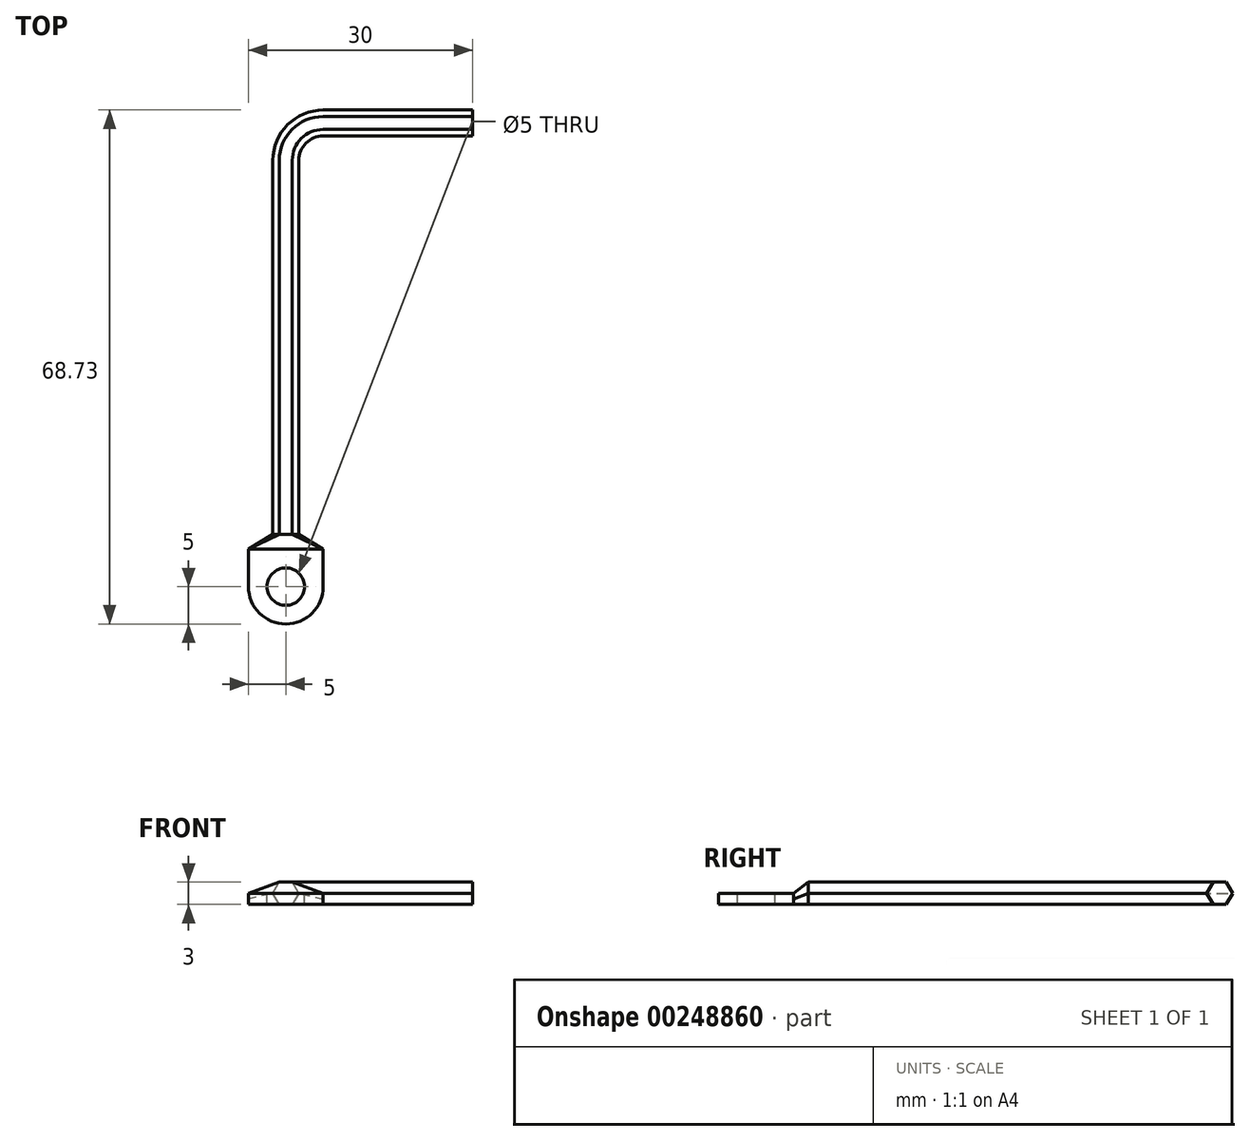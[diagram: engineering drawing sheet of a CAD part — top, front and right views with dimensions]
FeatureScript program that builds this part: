
annotation { "Feature Type Name" : "Feature", "Feature Type Description" : "" }
export const myFeature = defineFeature(function(context is Context, id is Id, definition is map)
    precondition{}
    {
        {
            var Q0;
            Q0=qCreatedBy(makeId("Front.planeOp"),FACE);
            var sketch = newSketch(context, id + "F0", { "sketchPlane" : qUnion([Q0])});
            skCircle(sketch, "E0.cCircle", {"center": v(0, 0) * mm, "radius": 1.5 * mm, "construction": true});
            skLineSegment(sketch, "E0.0", {"start": v(0.87, -1.5) * mm, "end": v(-0.87, -1.5) * mm});
            skLineSegment(sketch, "E0.1", {"start": v(-0.87, -1.5) * mm, "end": v(-1.73, 0) * mm});
            skLineSegment(sketch, "E0.2", {"start": v(-1.73, 0) * mm, "end": v(-0.87, 1.5) * mm});
            skLineSegment(sketch, "E0.3", {"start": v(-0.87, 1.5) * mm, "end": v(0.87, 1.5) * mm});
            skLineSegment(sketch, "E0.4", {"start": v(0.87, 1.5) * mm, "end": v(1.73, 0) * mm});
            skLineSegment(sketch, "E0.5", {"start": v(1.73, 0) * mm, "end": v(0.87, -1.5) * mm});
            skPoint(sketch, "E0.0.midPoint", {"position": v(0, -1.5) * mm});
            skSolve(sketch);
        }
        {
            var Q0;
            Q0=qCreatedBy(makeId("Top.planeOp"),FACE);
            var sketch = newSketch(context, id + "F1", { "sketchPlane" : qUnion([Q0])});
            skLineSegment(sketch, "E1", {"start": v(0, 0) * mm, "end": v(0, 50) * mm});
            skLineSegment(sketch, "E2", {"start": v(5, 55) * mm, "end": v(25, 55) * mm});
            skPoint(sketch, "E3.visualSharp", {"position": v(0, 55) * mm});
            skArc(sketch, "E3.filletArc", {"start": v(5, 55) * mm, "mid": v(1.46, 53.54) * mm, "end": v(0, 50) * mm});
            skSolve(sketch);
        }
        {
            var Q0;
            Q0 = qSketchRegion(id + "F0", true);
            var Q1;
            Q1 = qConstructionFilter(qBodyType(qCreatedBy(id + "F1" ,EDGE), BodyType.WIRE), ConstructionObject.NO);
            sweep(context, id + "F2", {"profiles" : qUnion([Q0]), "path" : qUnion([Q1])});
        }
        {
            var Q0;
            Q0=makeQuery(id+"F2.opSweep","CAP_FACE",FACE,{"disambiguationData":[OSD([sQuery(id+"F0.wireOp",EDGE,"E0.0"),sQuery(id+"F0.wireOp",EDGE,"E0.1"),sQuery(id+"F0.wireOp",EDGE,"E0.2"),sQuery(id+"F0.wireOp",EDGE,"E0.3"),sQuery(id+"F0.wireOp",EDGE,"E0.4"),sQuery(id+"F0.wireOp",EDGE,"E0.5"),sQuery(id+"F1.wireOp",VERTEX,"E1.start")])],"isStart":true});
            cPlane(context, id + "F3", {"entities" : qUnion([Q0]), "cplaneType" : CPlaneType.OFFSET, "offset" : 2 * mm, "width" : 150 * mm, "height" : 150 * mm});
        }
        {
            var Q0;
            Q0=qCreatedBy(id+"F3.planeOp",FACE);
            var sketch = newSketch(context, id + "F4", { "sketchPlane" : qUnion([Q0])});
            skLineSegment(sketch, "E4.bottom", {"start": v(-5, 0) * mm, "end": v(5, 0) * mm});
            skLineSegment(sketch, "E4.top", {"start": v(-5, -1.5) * mm, "end": v(5, -1.5) * mm});
            skLineSegment(sketch, "E4.left", {"start": v(-5, 0) * mm, "end": v(-5, -1.5) * mm});
            skLineSegment(sketch, "E4.right", {"start": v(5, 0) * mm, "end": v(5, -1.5) * mm});
            skSolve(sketch);
        }
        {
            var Q0;
            Q0 = qSketchRegion(id + "F4", true);
            extrude(context, id + "F5", {"entities" : qUnion([Q0]), "depth" : 10 * mm});
        }
        {
            var Q0;
            Q0=makeQuery(id+"F5.opExtrude","SWEPT_FACE",FACE,{"disambiguationData":[OSD([sQuery(id+"F4.wireOp",EDGE,"E4.bottom")])]});
            var sketch = newSketch(context, id + "F6", { "sketchPlane" : qUnion([Q0])});
            skCircle(sketch, "E5", {"center": v(0, -7) * mm, "radius": 2.5 * mm});
            skPoint(sketch, "E5.centerSnap0", {"position": v(-5, -7) * mm});
            skPoint(sketch, "E5.centerSnap1", {"position": v(0, -12) * mm});
            skSolve(sketch);
        }
        {
            var Q0;
            Q0 = qSketchRegion(id + "F6", true);
            extrude(context, id + "F7", {"entities" : qUnion([Q0]), "operationType" : NewBodyOperationType.REMOVE, "oppositeDirection" : true, "depth" : 25 * mm});
        }
        {
            var Q0;
            Q0=makeQuery(id+"F5.opExtrude","CAP_FACE",FACE,{"disambiguationData":[OSD([sQuery(id+"F4.wireOp",EDGE,"E4.bottom"),sQuery(id+"F4.wireOp",EDGE,"E4.top"),sQuery(id+"F4.wireOp",EDGE,"E4.left"),sQuery(id+"F4.wireOp",EDGE,"E4.right")])],"isStart":true});
            var sketch = newSketch(context, id + "F8", { "sketchPlane" : qUnion([Q0])});
            skLineSegment(sketch, "E6", {"start": v(-5, 0) * mm, "end": v(5, 0) * mm});
            skLineSegment(sketch, "E7", {"start": v(5, 0) * mm, "end": v(5, -0.75) * mm});
            skLineSegment(sketch, "E8", {"start": v(5, -0.75) * mm, "end": v(5, -1.5) * mm});
            skLineSegment(sketch, "E9", {"start": v(5, -1.5) * mm, "end": v(-5, -1.5) * mm});
            skLineSegment(sketch, "E10", {"start": v(-5, -1.5) * mm, "end": v(-5, -0.75) * mm});
            skLineSegment(sketch, "E11", {"start": v(-5, -0.75) * mm, "end": v(-5, 0) * mm});
            skSolve(sketch);
        }
        {
            var Q0;
            Q0=makeQuery(id+"F2.opSweep","CAP_FACE",FACE,{"disambiguationData":[OSD([sQuery(id+"F0.wireOp",EDGE,"E0.0"),sQuery(id+"F0.wireOp",EDGE,"E0.1"),sQuery(id+"F0.wireOp",EDGE,"E0.2"),sQuery(id+"F0.wireOp",EDGE,"E0.3"),sQuery(id+"F0.wireOp",EDGE,"E0.4"),sQuery(id+"F0.wireOp",EDGE,"E0.5"),sQuery(id+"F1.wireOp",VERTEX,"E1.start")])],"isStart":true});
            var Q1;
            Q1=makeQuery(id+"F8.imprint","IMPRINT",FACE,{"disambiguationData":[TD([[makeQuery(id+"F8.imprint","IMPRINT",EDGE,{"derivedFrom":sQuery(id+"F8.wireOp",EDGE,"E6")}),1.0]])]});
            loft(context, id + "F9", {"sheetProfilesArray" : [{ "sheetProfileEntities" : qUnion([Q0]) }, { "sheetProfileEntities" : qUnion([Q1]) }]});
        }
        {
            var Q0;
            Q0=makeQuery(id+"F5.opExtrude","CAP_EDGE",EDGE,{"disambiguationData":[OSD([sQuery(id+"F4.wireOp",EDGE,"E4.right")])],"isStart":false});
            var Q1;
            Q1=makeQuery(id+"F5.opExtrude","CAP_EDGE",EDGE,{"disambiguationData":[OSD([sQuery(id+"F4.wireOp",EDGE,"E4.left")])],"isStart":false});
            fillet(context, id + "F10", {"entities" : qUnion([Q0, Q1]), "radius" : 5 * mm, "tangentPropagation" : true, "allowEdgeOverflow" : false});
        }
    });
